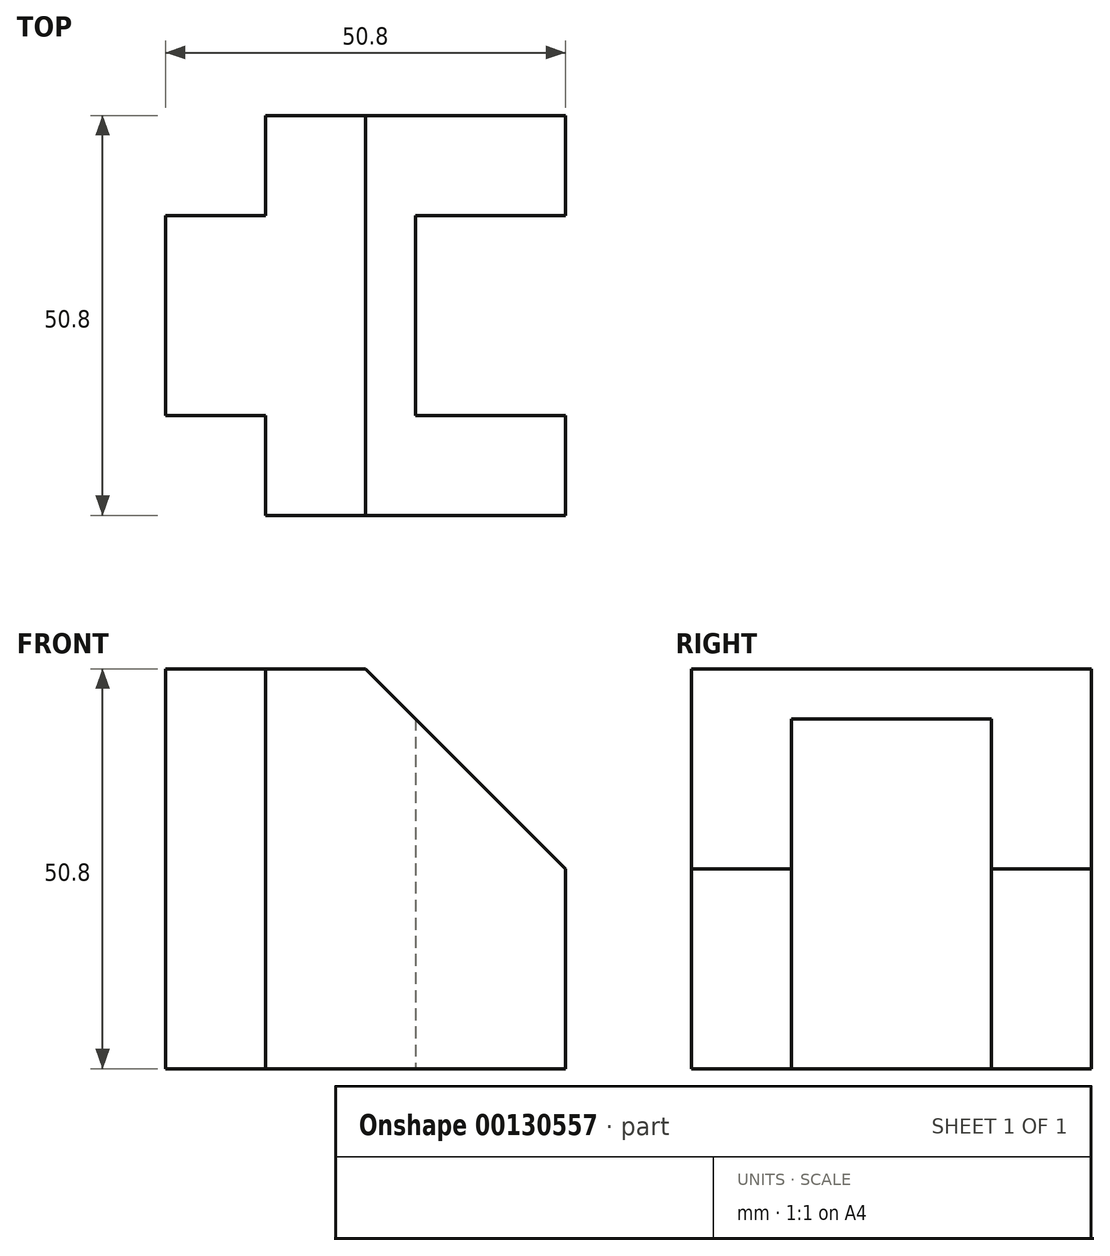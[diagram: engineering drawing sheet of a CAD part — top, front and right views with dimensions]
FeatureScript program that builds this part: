
annotation { "Feature Type Name" : "Feature", "Feature Type Description" : "" }
export const myFeature = defineFeature(function(context is Context, id is Id, definition is map)
    precondition{}
    {
        {
            var Q0;
            Q0=qCreatedBy(makeId("Front.planeOp"),FACE);
            var sketch = newSketch(context, id + "F0", { "sketchPlane" : qUnion([Q0])});
            skLineSegment(sketch, "E0.bottom", {"start": v(0, 0) * mm, "end": v(50.8, 0) * mm});
            skLineSegment(sketch, "E0.top", {"start": v(0, 50.8) * mm, "end": v(50.8, 50.8) * mm});
            skLineSegment(sketch, "E0.left", {"start": v(0, 0) * mm, "end": v(0, 50.8) * mm});
            skLineSegment(sketch, "E0.right", {"start": v(50.8, 0) * mm, "end": v(50.8, 50.8) * mm});
            skLineSegment(sketch, "E1", {"start": v(25.4, 50.8) * mm, "end": v(50.8, 25.4) * mm});
            skLineSegment(sketch, "E2", {"start": v(50.8, 25.4) * mm, "end": v(50.8, 50.8) * mm});
            skLineSegment(sketch, "E3", {"start": v(50.8, 50.8) * mm, "end": v(25.4, 50.8) * mm});
            skSolve(sketch);
        }
        {
            var Q0;
            Q0=makeQuery(id+"F0.imprint","IMPRINT",FACE,{"disambiguationData":[TD([[makeQuery(id+"F0.imprint","IMPRINT",EDGE,{"derivedFrom":sQuery(id+"F0.wireOp",EDGE,"E0.bottom")}),1.0]])]});
            extrude(context, id + "F1", {"entities" : qUnion([Q0]), "oppositeDirection" : true, "depth" : 50.8 * mm});
        }
        {
            var Q0;
            Q0=makeQuery(id+"F1.opExtrude","SWEPT_FACE",FACE,{"disambiguationData":[OSD([sQuery(id+"F0.wireOp",EDGE,"E0.bottom")])]});
            var sketch = newSketch(context, id + "F2", { "sketchPlane" : qUnion([Q0])});
            skLineSegment(sketch, "E4.bottom", {"start": v(50.8, -12.7) * mm, "end": v(31.75, -12.7) * mm});
            skLineSegment(sketch, "E4.top", {"start": v(50.8, -38.1) * mm, "end": v(31.75, -38.1) * mm});
            skLineSegment(sketch, "E4.left", {"start": v(50.8, -12.7) * mm, "end": v(50.8, -38.1) * mm});
            skLineSegment(sketch, "E4.right", {"start": v(31.75, -12.7) * mm, "end": v(31.75, -38.1) * mm});
            skLineSegment(sketch, "E5.bottom", {"start": v(0, 0) * mm, "end": v(12.7, 0) * mm});
            skLineSegment(sketch, "E5.top", {"start": v(0, -12.7) * mm, "end": v(12.7, -12.7) * mm});
            skLineSegment(sketch, "E5.left", {"start": v(0, 0) * mm, "end": v(0, -12.7) * mm});
            skLineSegment(sketch, "E5.right", {"start": v(12.7, 0) * mm, "end": v(12.7, -12.7) * mm});
            skLineSegment(sketch, "E6.bottom", {"start": v(0, -50.8) * mm, "end": v(12.7, -50.8) * mm});
            skLineSegment(sketch, "E6.top", {"start": v(0, -38.1) * mm, "end": v(12.7, -38.1) * mm});
            skLineSegment(sketch, "E6.left", {"start": v(0, -50.8) * mm, "end": v(0, -38.1) * mm});
            skLineSegment(sketch, "E6.right", {"start": v(12.7, -50.8) * mm, "end": v(12.7, -38.1) * mm});
            skSolve(sketch);
        }
        {
            var Q0;
            Q0=makeQuery(id+"F2.imprint","IMPRINT",FACE,{"disambiguationData":[TD([[makeQuery(id+"F2.imprint","IMPRINT",EDGE,{"derivedFrom":sQuery(id+"F2.wireOp",EDGE,"E4.bottom")}),1.0]])]});
            var Q1;
            Q1=makeQuery(id+"F2.imprint","IMPRINT",FACE,{"disambiguationData":[TD([[makeQuery(id+"F2.imprint","IMPRINT",EDGE,{"derivedFrom":sQuery(id+"F2.wireOp",EDGE,"E5.bottom")}),-1.0]])]});
            var Q2;
            Q2=makeQuery(id+"F2.imprint","IMPRINT",FACE,{"disambiguationData":[TD([[makeQuery(id+"F2.imprint","IMPRINT",EDGE,{"derivedFrom":sQuery(id+"F2.wireOp",EDGE,"E6.bottom")}),1.0]])]});
            extrude(context, id + "F3", {"entities" : qUnion([Q0, Q1, Q2]), "operationType" : NewBodyOperationType.REMOVE, "endBound" : BoundingType.THROUGH_ALL, "oppositeDirection" : true, "depth" : 25.4 * mm});
        }
    });
